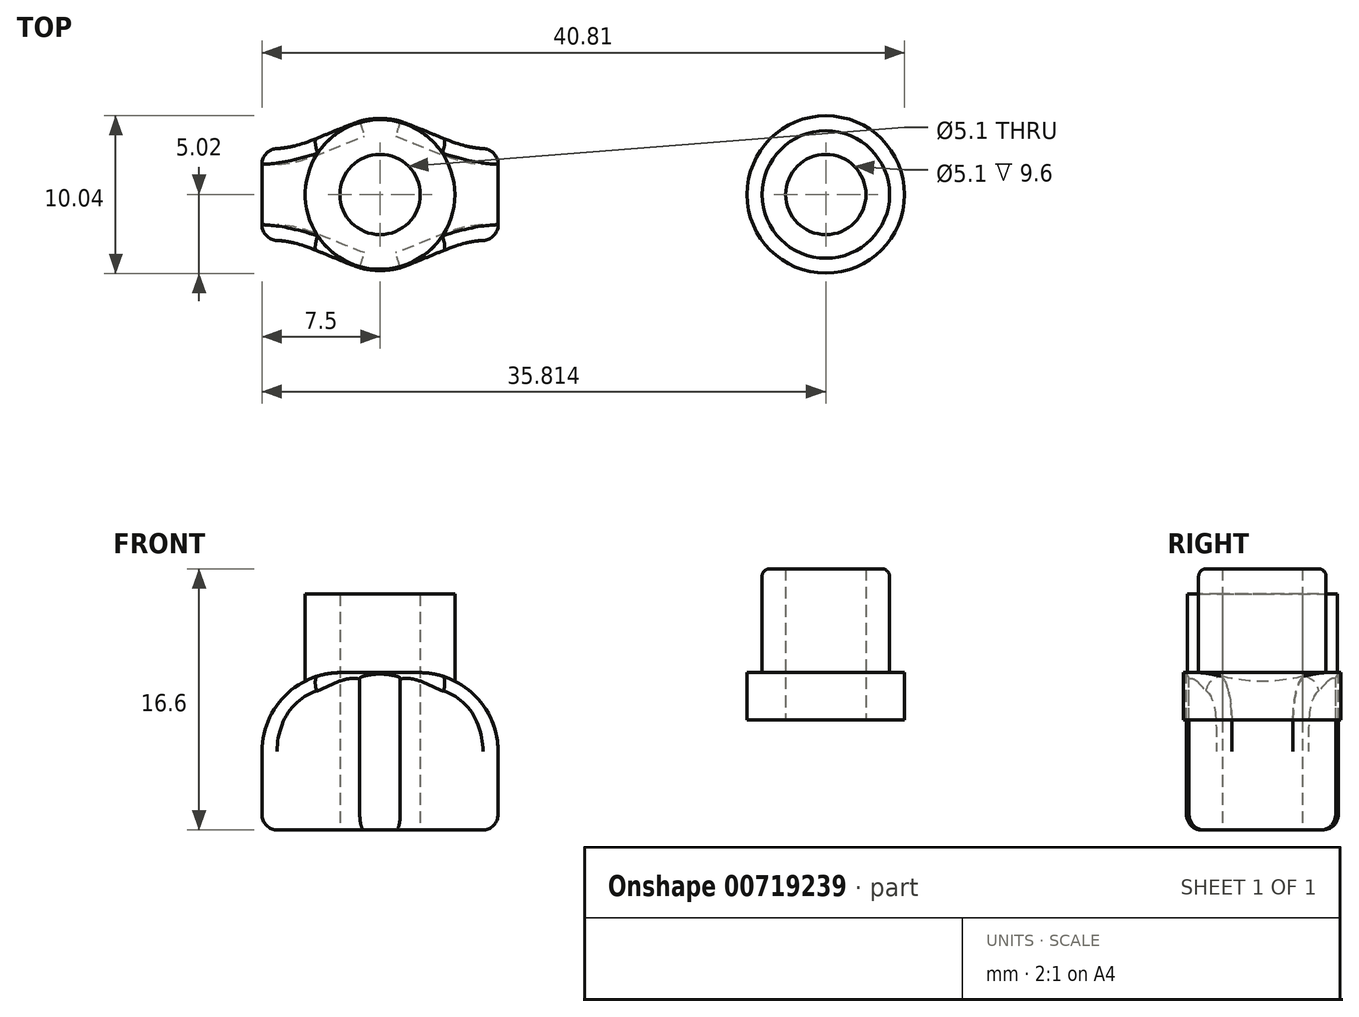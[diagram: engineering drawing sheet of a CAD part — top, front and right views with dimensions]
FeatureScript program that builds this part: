
annotation { "Feature Type Name" : "Feature", "Feature Type Description" : "" }
export const myFeature = defineFeature(function(context is Context, id is Id, definition is map)
    precondition{}
    {
        {
            var Q0;
            Q0=qCreatedBy(makeId("Top.planeOp"),FACE);
            var sketch = newSketch(context, id + "F0", { "sketchPlane" : qUnion([Q0])});
            skLineSegment(sketch, "E0.bottom", {"start": v(-7.5, 5) * mm, "end": v(7.5, 5) * mm, "construction": true});
            skLineSegment(sketch, "E0.top", {"start": v(-7.5, -5) * mm, "end": v(7.5, -5) * mm, "construction": true});
            skLineSegment(sketch, "E0.left", {"start": v(-7.5, 5) * mm, "end": v(-7.5, -5) * mm});
            skLineSegment(sketch, "E0.right", {"start": v(7.5, 5) * mm, "end": v(7.5, -5) * mm});
            skLineSegment(sketch, "E1", {"start": v(0, 5) * mm, "end": v(0, -5) * mm, "construction": true});
            skLineSegment(sketch, "E2", {"start": v(-7.5, 0) * mm, "end": v(7.5, 0) * mm, "construction": true});
            skCircle(sketch, "E3", {"center": v(0, 0) * mm, "radius": 2.55 * mm});
            skCircle(sketch, "E4", {"center": v(28.31, 0) * mm, "radius": 4.05 * mm});
            skCircle(sketch, "E5", {"center": v(28.31, 0) * mm, "radius": 2.55 * mm});
            skCircle(sketch, "E6", {"center": v(28.31, 0) * mm, "radius": 5 * mm});
            skLineSegment(sketch, "E7", {"start": v(1.29, 4.66) * mm, "end": v(7.5, 3) * mm, "construction": true});
            skLineSegment(sketch, "E8.MirrorCS", {"start": v(1.29, -4.66) * mm, "end": v(7.5, -3) * mm, "construction": true});
            skLineSegment(sketch, "E9.MirrorCS", {"start": v(-1.29, 4.66) * mm, "end": v(-7.5, 3) * mm, "construction": true});
            skLineSegment(sketch, "E10.MirrorCS", {"start": v(-1.29, -4.66) * mm, "end": v(-7.5, -3) * mm, "construction": true});
            skCircle(sketch, "E11", {"center": v(0, 0) * mm, "radius": 4.75 * mm});
            skPoint(sketch, "E12.visualSharp", {"position": v(0, -5) * mm});
            skArc(sketch, "E12.filletArc", {"start": v(-1.29, -4.66) * mm, "mid": v(0, -4.83) * mm, "end": v(1.29, -4.66) * mm});
            skPoint(sketch, "E13.visualSharp", {"position": v(0, 5) * mm});
            skArc(sketch, "E13.filletArc", {"start": v(1.29, 4.66) * mm, "mid": v(0, 4.83) * mm, "end": v(-1.29, 4.66) * mm});
            skFitSpline(sketch, "E14", {"points": [v(1.29, -4.66) * mm, v(7.5, -3) * mm], "startDerivative": vector(7.76, 2.75) * mm, "endDerivative": vector(5.93, -1.19) * mm});
            skFitSpline(sketch, "E15.MirrorCS", {"points": [v(1.29, 4.66) * mm, v(7.5, 3) * mm], "startDerivative": vector(7.76, -2.75) * mm, "endDerivative": vector(5.93, 1.19) * mm});
            skFitSpline(sketch, "E16.MirrorCS", {"points": [v(-1.29, 4.66) * mm, v(-7.5, 3) * mm], "startDerivative": vector(-7.76, -2.75) * mm, "endDerivative": vector(-5.93, 1.19) * mm});
            skFitSpline(sketch, "E17.MirrorCS", {"points": [v(-1.29, -4.66) * mm, v(-7.5, -3) * mm], "startDerivative": vector(-7.76, 2.75) * mm, "endDerivative": vector(-5.93, -1.19) * mm});
            skSolve(sketch);
        }
        {
            var Q0;
            Q0=makeQuery(id+"F0.imprint","IMPRINT",FACE,{"disambiguationData":[TD([[makeQuery(id+"F0.imprint","IMPRINT",EDGE,{"derivedFrom":sQuery(id+"F0.wireOp",EDGE,"E4")}),1.0]])]});
            extrude(context, id + "F1", {"entities" : qUnion([Q0]), "depth" : 6.6 * mm, "offsetDistance" : 25 * mm});
        }
        {
            var Q0;
            Q0=makeQuery(id+"F0.imprint","IMPRINT",FACE,{"disambiguationData":[TD([[makeQuery(id+"F0.imprint","IMPRINT",EDGE,{"derivedFrom":sQuery(id+"F0.wireOp",EDGE,"E3")}),-1.0]])]});
            extrude(context, id + "F2", {"entities" : qUnion([Q0]), "depth" : 5 * mm, "offsetDistance" : 25 * mm});
        }
        {
            var Q0;
            Q0=makeQuery(id+"F0.imprint","IMPRINT",FACE,{"disambiguationData":[TD([[makeQuery(id+"F0.imprint","IMPRINT",EDGE,{"derivedFrom":sQuery(id+"F0.wireOp",EDGE,"E3")}),-1.0]])]});
            var Q1;
            Q1=makeQuery(id+"F0.imprint","IMPRINT",FACE,{"disambiguationData":[TD([[makeQuery(id+"F0.imprint","IMPRINT",EDGE,{"derivedFrom":sQuery(id+"F0.wireOp",EDGE,"E11")}),-1.0]])]});
            extrude(context, id + "F3", {"entities" : qUnion([Q0, Q1]), "operationType" : NewBodyOperationType.ADD, "oppositeDirection" : true, "depth" : 10 * mm, "offsetDistance" : 25 * mm});
        }
        {
            var Q0;
            Q0=makeQuery(id+"F3.opExtrude","CAP_EDGE",EDGE,{"disambiguationData":[OSD([sQuery(id+"F0.wireOp",EDGE,"E0.left")])],"isStart":true});
            var Q1;
            Q1=makeQuery(id+"F3.opExtrude","CAP_EDGE",EDGE,{"disambiguationData":[OSD([sQuery(id+"F0.wireOp",EDGE,"E0.right")])],"isStart":true});
            fillet(context, id + "F4", {"entities" : qUnion([Q0, Q1]), "radius" : 5 * mm, "tangentPropagation" : true, "allowEdgeOverflow" : false});
        }
        {
            var Q0;
            Q0=makeQuery(id+"F3.opExtrude","CAP_EDGE",EDGE,{"disambiguationData":[OSD([sQuery(id+"F0.wireOp",EDGE,"E0.left")])],"isStart":false});
            var Q1;
            Q1=makeQuery(id+"F3.opExtrude","CAP_EDGE",EDGE,{"disambiguationData":[OSD([sQuery(id+"F0.wireOp",EDGE,"E0.right")])],"isStart":false});
            var Q2;
            Q2=makeQuery(id+"F3.opExtrude","CAP_EDGE",EDGE,{"disambiguationData":[OSD([sQuery(id+"F0.wireOp",EDGE,"E8.MirrorCS")])],"isStart":false});
            var Q3;
            Q3=makeQuery(id+"F3.opExtrude","CAP_EDGE",EDGE,{"disambiguationData":[OSD([sQuery(id+"F0.wireOp",EDGE,"E10.MirrorCS")])],"isStart":false});
            var Q4;
            Q4=makeQuery(id+"F3.opExtrude","CAP_EDGE",EDGE,{"disambiguationData":[OSD([sQuery(id+"F0.wireOp",EDGE,"E9.MirrorCS")])],"isStart":false});
            var Q5;
            Q5=makeQuery(id+"F3.opExtrude","CAP_EDGE",EDGE,{"disambiguationData":[OSD([sQuery(id+"F0.wireOp",EDGE,"E7")])],"isStart":false});
            var Q6;
            Q6=makeQuery(id+"F3.opExtrude","SWEPT_EDGE",EDGE,{"disambiguationData":[OSD([sQuery(id+"F0.wireOp",EDGE,"E0.right"),sQuery(id+"F0.wireOp",EDGE,"E7")])]});
            var Q7;
            Q7=makeQuery(id+"F3.opExtrude","SWEPT_EDGE",EDGE,{"disambiguationData":[OSD([sQuery(id+"F0.wireOp",EDGE,"E0.right"),sQuery(id+"F0.wireOp",EDGE,"E8.MirrorCS")])]});
            var Q8;
            Q8=makeQuery(id+"F3.opExtrude","SWEPT_EDGE",EDGE,{"disambiguationData":[OSD([sQuery(id+"F0.wireOp",EDGE,"E0.left"),sQuery(id+"F0.wireOp",EDGE,"E10.MirrorCS")])]});
            var Q9;
            Q9=makeQuery(id+"F3.opExtrude","SWEPT_EDGE",EDGE,{"disambiguationData":[OSD([sQuery(id+"F0.wireOp",EDGE,"E0.left"),sQuery(id+"F0.wireOp",EDGE,"E9.MirrorCS")])]});
            var Q10;
            Q10=makeQuery(id+"F3.opExtrude","CAP_EDGE",EDGE,{"disambiguationData":[OSD([sQuery(id+"F0.wireOp",EDGE,"E17.MirrorCS")])],"isStart":false});
            var Q11;
            Q11=makeQuery(id+"F3.opExtrude","CAP_EDGE",EDGE,{"disambiguationData":[OSD([sQuery(id+"F0.wireOp",EDGE,"E12.filletArc")])],"isStart":false});
            var Q12;
            Q12=makeQuery(id+"F3.opExtrude","CAP_EDGE",EDGE,{"disambiguationData":[OSD([sQuery(id+"F0.wireOp",EDGE,"E14")])],"isStart":false});
            var Q13;
            Q13=makeQuery(id+"F3.opExtrude","CAP_EDGE",EDGE,{"disambiguationData":[OSD([sQuery(id+"F0.wireOp",EDGE,"E15.MirrorCS")])],"isStart":false});
            var Q14;
            Q14=makeQuery(id+"F3.opExtrude","CAP_EDGE",EDGE,{"disambiguationData":[OSD([sQuery(id+"F0.wireOp",EDGE,"E13.filletArc")])],"isStart":false});
            var Q15;
            Q15=makeQuery(id+"F3.opExtrude","CAP_EDGE",EDGE,{"disambiguationData":[OSD([sQuery(id+"F0.wireOp",EDGE,"E16.MirrorCS")])],"isStart":false});
            fillet(context, id + "F5", {"entities" : qUnion([Q0, Q1, Q2, Q3, Q4, Q5, Q6, Q7, Q8, Q9, Q10, Q11, Q12, Q13, Q14, Q15]), "radius" : 1 * mm, "tangentPropagation" : true, "allowEdgeOverflow" : false});
        }
        {
            var Q0;
            Q0=makeQuery(id+"F0.imprint","IMPRINT",FACE,{"disambiguationData":[TD([[makeQuery(id+"F0.imprint","IMPRINT",EDGE,{"derivedFrom":sQuery(id+"F0.wireOp",EDGE,"E4")}),-1.0]])]});
            var Q1;
            Q1=makeQuery(id+"F0.imprint","IMPRINT",FACE,{"disambiguationData":[TD([[makeQuery(id+"F0.imprint","IMPRINT",EDGE,{"derivedFrom":sQuery(id+"F0.wireOp",EDGE,"E4")}),1.0]])]});
            extrude(context, id + "F6", {"entities" : qUnion([Q0, Q1]), "operationType" : NewBodyOperationType.ADD, "oppositeDirection" : true, "depth" : 3 * mm, "offsetDistance" : 25 * mm});
        }
        {
            var Q0;
            Q0=makeQuery(id+"F1.opExtrude","CAP_EDGE",EDGE,{"disambiguationData":[OSD([sQuery(id+"F0.wireOp",EDGE,"E4")])],"isStart":false});
            fillet(context, id + "F7", {"entities" : qUnion([Q0]), "radius" : 0.5 * mm, "tangentPropagation" : true, "allowEdgeOverflow" : false});
        }
    });
